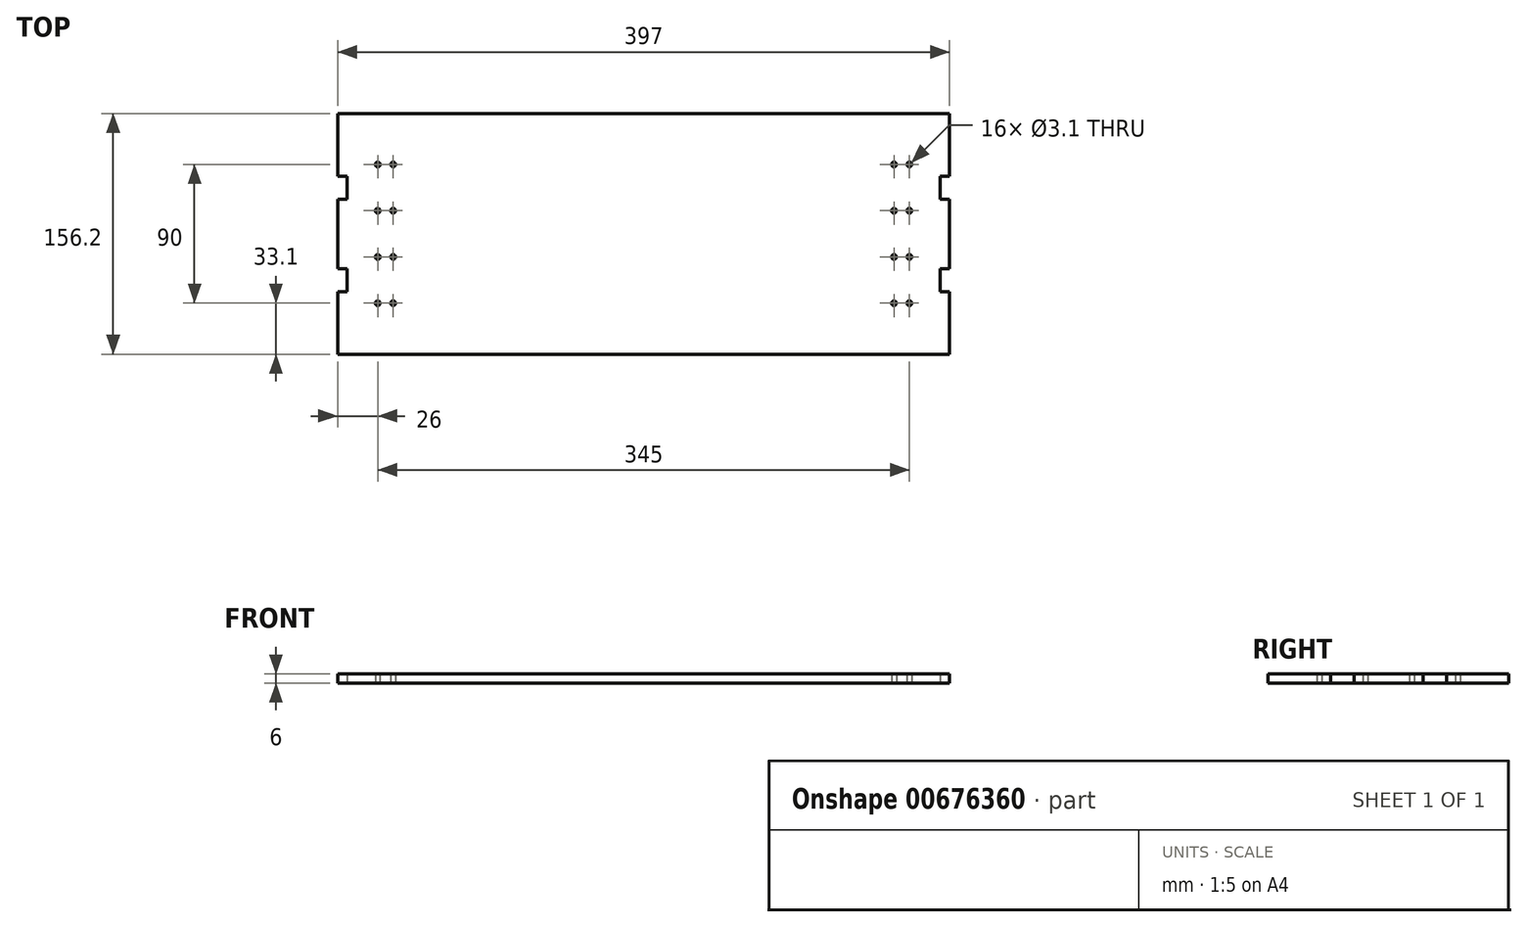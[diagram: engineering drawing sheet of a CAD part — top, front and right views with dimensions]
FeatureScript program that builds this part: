
annotation { "Feature Type Name" : "Feature", "Feature Type Description" : "" }
export const myFeature = defineFeature(function(context is Context, id is Id, definition is map)
    precondition{}
    {
        {
            var Q0;
            Q0=qCreatedBy(makeId("Top.planeOp"),FACE);
            var sketch = newSketch(context, id + "F0", { "sketchPlane" : qUnion([Q0])});
            skLineSegment(sketch, "E0.bottom", {"start": v(0, 0) * mm, "end": v(-397, 0) * mm});
            skLineSegment(sketch, "E0.top", {"start": v(0, 156.2) * mm, "end": v(-397, 156.2) * mm});
            skLineSegment(sketch, "E0.left", {"start": v(0, 0) * mm, "end": v(0, 156.2) * mm});
            skLineSegment(sketch, "E0.right", {"start": v(-397, 0) * mm, "end": v(-397, 156.2) * mm});
            skLineSegment(sketch, "E1", {"start": v(-397, 40.6) * mm, "end": v(-391, 40.6) * mm});
            skLineSegment(sketch, "E2", {"start": v(-391, 40.6) * mm, "end": v(-391, 55.6) * mm});
            skLineSegment(sketch, "E3", {"start": v(-391, 55.6) * mm, "end": v(-397, 55.6) * mm});
            skLineSegment(sketch, "E4", {"start": v(-397, 100.6) * mm, "end": v(-391, 100.6) * mm});
            skLineSegment(sketch, "E5", {"start": v(-391, 100.6) * mm, "end": v(-391, 115.6) * mm});
            skLineSegment(sketch, "E6", {"start": v(-391, 115.6) * mm, "end": v(-397, 115.6) * mm});
            skLineSegment(sketch, "E7", {"start": v(-198.5, 209.54) * mm, "end": v(-198.5, -21.9) * mm, "construction": true});
            skPoint(sketch, "E7.startSnap0", {"position": v(-198.5, 156.2) * mm});
            skLineSegment(sketch, "E8.MirrorCS", {"start": v(-6, 115.6) * mm, "end": v(0, 115.6) * mm});
            skLineSegment(sketch, "E9.MirrorCS", {"start": v(-6, 100.6) * mm, "end": v(-6, 115.6) * mm});
            skLineSegment(sketch, "E10.MirrorCS", {"start": v(0, 100.6) * mm, "end": v(-6, 100.6) * mm});
            skLineSegment(sketch, "E11.MirrorCS", {"start": v(-6, 55.6) * mm, "end": v(0, 55.6) * mm});
            skLineSegment(sketch, "E12.MirrorCS", {"start": v(0, 40.6) * mm, "end": v(-6, 40.6) * mm});
            skLineSegment(sketch, "E13.MirrorCS", {"start": v(-6, 40.6) * mm, "end": v(-6, 55.6) * mm});
            skPoint(sketch, "E14.centerSnap0", {"position": v(-391, 108.1) * mm});
            skPoint(sketch, "E15.centerSnap0", {"position": v(-391, 48.1) * mm});
            skCircle(sketch, "E16", {"center": v(-371, 123.1) * mm, "radius": 1.55 * mm});
            skCircle(sketch, "E17", {"center": v(-371, 93.1) * mm, "radius": 1.55 * mm});
            skCircle(sketch, "E18", {"center": v(-371, 63.1) * mm, "radius": 1.55 * mm});
            skCircle(sketch, "E19", {"center": v(-371, 33.1) * mm, "radius": 1.55 * mm});
            skCircle(sketch, "E20.MirrorC", {"center": v(-26, 123.1) * mm, "radius": 1.55 * mm});
            skCircle(sketch, "E21.MirrorC", {"center": v(-26, 93.1) * mm, "radius": 1.55 * mm});
            skCircle(sketch, "E22.MirrorC", {"center": v(-26, 33.1) * mm, "radius": 1.55 * mm});
            skCircle(sketch, "E23.MirrorC", {"center": v(-26, 63.1) * mm, "radius": 1.55 * mm});
            skCircle(sketch, "E24", {"center": v(-361, 123.1) * mm, "radius": 1.55 * mm});
            skCircle(sketch, "E25", {"center": v(-361, 93.1) * mm, "radius": 1.55 * mm});
            skCircle(sketch, "E26", {"center": v(-361, 63.1) * mm, "radius": 1.55 * mm});
            skCircle(sketch, "E27", {"center": v(-361, 33.1) * mm, "radius": 1.55 * mm});
            skCircle(sketch, "E28.MirrorC", {"center": v(-36, 123.1) * mm, "radius": 1.55 * mm});
            skCircle(sketch, "E29.MirrorC", {"center": v(-36, 93.1) * mm, "radius": 1.55 * mm});
            skCircle(sketch, "E30.MirrorC", {"center": v(-36, 63.1) * mm, "radius": 1.55 * mm});
            skCircle(sketch, "E31.MirrorC", {"center": v(-36, 33.1) * mm, "radius": 1.55 * mm});
            skSolve(sketch);
        }
        {
            var Q0;
            {var subQ3=sQuery(id+"F0.wireOp",EDGE,"E0.bottom");Q0=makeQuery(id+"F0.imprint","IMPRINT",FACE,{"disambiguationData":[TD([[makeQuery(id+"F0.imprint","IMPRINT",EDGE,{"derivedFrom":subQ3}),-1.0]])]});}
            extrude(context, id + "F1", {"entities" : qUnion([Q0]), "depth" : 6 * mm, "offsetDistance" : 25 * mm});
        }
    });
